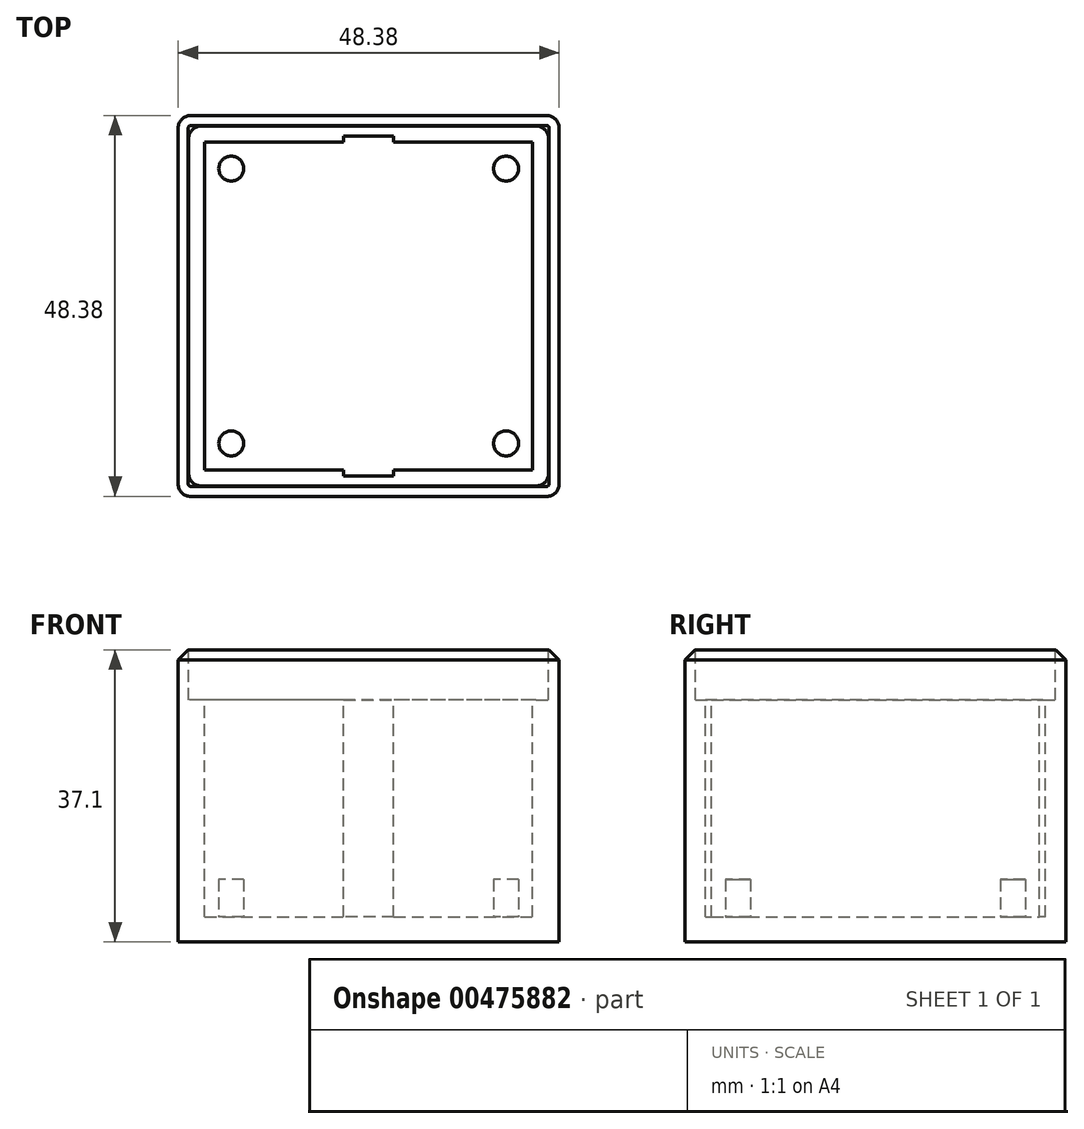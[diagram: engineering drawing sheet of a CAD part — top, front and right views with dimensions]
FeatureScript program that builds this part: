
annotation { "Feature Type Name" : "Feature", "Feature Type Description" : "" }
export const myFeature = defineFeature(function(context is Context, id is Id, definition is map)
    precondition{}
    {
        {
            var Q0;
            Q0=qCreatedBy(makeId("Top.planeOp"),FACE);
            var sketch = newSketch(context, id + "F0", { "sketchPlane" : qUnion([Q0])});
            skLineSegment(sketch, "E0.bottom", {"start": v(22.6, 24.2) * mm, "end": v(-22.6, 24.2) * mm});
            skLineSegment(sketch, "E0.top", {"start": v(22.6, -24.2) * mm, "end": v(-22.6, -24.2) * mm});
            skLineSegment(sketch, "E0.left", {"start": v(24.2, 22.6) * mm, "end": v(24.2, -22.6) * mm});
            skLineSegment(sketch, "E0.right", {"start": v(-24.2, 22.6) * mm, "end": v(-24.2, -22.6) * mm});
            skPoint(sketch, "E0.middle", {"position": v(0, 0) * mm});
            skPoint(sketch, "E1.visualSharp", {"position": v(-24.2, 24.2) * mm});
            skArc(sketch, "E1.filletArc", {"start": v(-22.6, 24.2) * mm, "mid": v(-23.73, 23.73) * mm, "end": v(-24.2, 22.6) * mm});
            skPoint(sketch, "E2.visualSharp", {"position": v(24.2, 24.2) * mm});
            skArc(sketch, "E2.filletArc", {"start": v(24.2, 22.6) * mm, "mid": v(23.73, 23.73) * mm, "end": v(22.6, 24.2) * mm});
            skPoint(sketch, "E3.visualSharp", {"position": v(24.2, -24.2) * mm});
            skArc(sketch, "E3.filletArc", {"start": v(22.6, -24.2) * mm, "mid": v(23.73, -23.73) * mm, "end": v(24.2, -22.6) * mm});
            skPoint(sketch, "E4.visualSharp", {"position": v(-24.2, -24.2) * mm});
            skArc(sketch, "E4.filletArc", {"start": v(-24.2, -22.6) * mm, "mid": v(-23.73, -23.73) * mm, "end": v(-22.6, -24.2) * mm});
            skSolve(sketch);
        }
        {
            var Q0;
            Q0 = qSketchRegion(id + "F0", true);
            extrude(context, id + "F1", {"entities" : qUnion([Q0]), "endBound" : BoundingType.SYMMETRIC, "depth" : 37.1 * mm});
        }
        {
            var Q0;
            Q0=makeQuery(id+"F1.opExtrude","CAP_FACE",FACE,{"disambiguationData":[OSD([sQuery(id+"F0.wireOp",EDGE,"E0.bottom"),sQuery(id+"F0.wireOp",EDGE,"E0.top"),sQuery(id+"F0.wireOp",EDGE,"E0.left"),sQuery(id+"F0.wireOp",EDGE,"E0.right"),sQuery(id+"F0.wireOp",EDGE,"E1.filletArc"),sQuery(id+"F0.wireOp",EDGE,"E2.filletArc"),sQuery(id+"F0.wireOp",EDGE,"E3.filletArc"),sQuery(id+"F0.wireOp",EDGE,"E4.filletArc")])],"isStart":false});
            var sketch = newSketch(context, id + "F2", { "sketchPlane" : qUnion([Q0])});
            skLineSegment(sketch, "E5.1", {"start": v(20.83, 20.38) * mm, "end": v(20.83, -20.38) * mm});
            skLineSegment(sketch, "E5.2", {"start": v(20.38, 20.83) * mm, "end": v(-20.38, 20.83) * mm});
            skLineSegment(sketch, "E5.5", {"start": v(-20.83, 20.38) * mm, "end": v(-20.83, -20.38) * mm});
            skLineSegment(sketch, "E5.7", {"start": v(20.38, -20.83) * mm, "end": v(-20.38, -20.83) * mm});
            skLineSegment(sketch, "E6", {"start": v(-20.83, 20.38) * mm, "end": v(-20.83, 20.83) * mm});
            skLineSegment(sketch, "E7", {"start": v(-20.83, 20.83) * mm, "end": v(-20.38, 20.83) * mm});
            skLineSegment(sketch, "E8", {"start": v(20.38, 20.83) * mm, "end": v(20.83, 20.83) * mm});
            skLineSegment(sketch, "E9", {"start": v(20.83, 20.83) * mm, "end": v(20.83, 20.38) * mm});
            skLineSegment(sketch, "E10", {"start": v(20.83, -20.38) * mm, "end": v(20.83, -20.83) * mm});
            skLineSegment(sketch, "E11", {"start": v(20.83, -20.83) * mm, "end": v(20.38, -20.83) * mm});
            skLineSegment(sketch, "E12", {"start": v(-20.83, -20.38) * mm, "end": v(-20.83, -20.83) * mm});
            skLineSegment(sketch, "E13", {"start": v(-20.83, -20.83) * mm, "end": v(-20.38, -20.83) * mm});
            skSolve(sketch);
        }
        {
            var Q0;
            Q0 = qSketchRegion(id + "F2", true);
            extrude(context, id + "F3", {"entities" : qUnion([Q0]), "operationType" : NewBodyOperationType.REMOVE, "oppositeDirection" : true, "depth" : 33.93 * mm});
        }
        {
            var Q0;
            Q0=makeQuery(id+"F1.opExtrude","CAP_FACE",FACE,{"disambiguationData":[OSD([sQuery(id+"F0.wireOp",EDGE,"E0.bottom"),sQuery(id+"F0.wireOp",EDGE,"E0.top"),sQuery(id+"F0.wireOp",EDGE,"E0.left"),sQuery(id+"F0.wireOp",EDGE,"E0.right"),sQuery(id+"F0.wireOp",EDGE,"E1.filletArc"),sQuery(id+"F0.wireOp",EDGE,"E2.filletArc"),sQuery(id+"F0.wireOp",EDGE,"E3.filletArc"),sQuery(id+"F0.wireOp",EDGE,"E4.filletArc")])],"isStart":false});
            var sketch = newSketch(context, id + "F4", { "sketchPlane" : qUnion([Q0])});
            skLineSegment(sketch, "E14.bottom", {"start": v(22.86, 22.86) * mm, "end": v(-22.86, 22.86) * mm});
            skLineSegment(sketch, "E14.top", {"start": v(22.86, -22.86) * mm, "end": v(-22.86, -22.86) * mm});
            skLineSegment(sketch, "E14.left", {"start": v(22.86, 22.86) * mm, "end": v(22.86, -22.86) * mm});
            skLineSegment(sketch, "E14.right", {"start": v(-22.86, 22.86) * mm, "end": v(-22.86, -22.86) * mm});
            skPoint(sketch, "E14.middle", {"position": v(0, 0) * mm});
            skSolve(sketch);
        }
        {
            var Q0;
            Q0 = qSketchRegion(id + "F4", true);
            extrude(context, id + "F5", {"entities" : qUnion([Q0]), "operationType" : NewBodyOperationType.REMOVE, "oppositeDirection" : true, "depth" : 6.35 * mm});
        }
        {
            var Q0;
            {var subQ0=sQuery(id+"F2.wireOp",EDGE,"E5.7");var subQ1=sQuery(id+"F2.wireOp",EDGE,"E5.6");var subQ2=sQuery(id+"F2.wireOp",EDGE,"E5.5");var subQ3=sQuery(id+"F2.wireOp",EDGE,"E5.4");var subQ4=sQuery(id+"F2.wireOp",EDGE,"E5.3");var subQ5=sQuery(id+"F2.wireOp",EDGE,"E5.2");var subQ6=sQuery(id+"F2.wireOp",EDGE,"E5.1");var subQ7=sQuery(id+"F2.wireOp",EDGE,"E5.0");Q0=makeQuery(id+"F6M7IgCAsm79SRp_1.boolean.opBoolean","MERGE",FACE,{"derivedFrom":[makeQuery(id+"F3.boolean.opBoolean","COPY",FACE,{"derivedFrom":makeQuery(id+"F3.opExtrude","CAP_FACE",FACE,{"disambiguationData":[OSD([subQ7,subQ6,subQ5,subQ4,subQ3,subQ2,subQ1,subQ0])],"isStart":false})}),makeQuery(id+"F6M7IgCAsm79SRp_1.opExtrude","CAP_FACE",FACE,{"disambiguationData":[OSD([subQ7,subQ6,subQ5,subQ4,subQ3,subQ2,subQ1,subQ0]),ownerDisambiguation([makeQuery(id+"FmsYwUqMiXvRgAx_1.imprint","IMPRINT",EDGE,{"derivedFrom":sQuery(id+"FmsYwUqMiXvRgAx_1.wireOp",EDGE,"RRrNXNMf-GQmn-cS1J-N3Tq-7I37AppBpzz9.bottom")})])],"isStart":false}),makeQuery(id+"F6M7IgCAsm79SRp_1.opExtrude","CAP_FACE",FACE,{"disambiguationData":[OSD([subQ7,subQ6,subQ5,subQ4,subQ3,subQ2,subQ1,subQ0]),ownerDisambiguation([makeQuery(id+"FmsYwUqMiXvRgAx_1.imprint","IMPRINT",EDGE,{"derivedFrom":sQuery(id+"FmsYwUqMiXvRgAx_1.wireOp",EDGE,"797062fd-0b08-47d3-9a36-d671014024f00.MirrorCS")})])],"isStart":false})]});}
            var sketch = newSketch(context, id + "F6", { "sketchPlane" : qUnion([Q0])});
            skCircle(sketch, "E15", {"center": v(17.45, -17.45) * mm, "radius": 1.59 * mm});
            skCircle(sketch, "E16.MirrorC", {"center": v(-17.45, -17.45) * mm, "radius": 1.59 * mm});
            skCircle(sketch, "E17.MirrorC", {"center": v(-17.45, 17.45) * mm, "radius": 1.59 * mm});
            skCircle(sketch, "E18.MirrorC", {"center": v(17.45, 17.45) * mm, "radius": 1.59 * mm});
            skLineSegment(sketch, "E19", {"start": v(20.83, -20.83) * mm, "end": v(17.45, -17.45) * mm, "construction": true});
            skSolve(sketch);
        }
        {
            var Q0;
            Q0 = qSketchRegion(id + "F6", true);
            extrude(context, id + "F7", {"entities" : qUnion([Q0]), "operationType" : NewBodyOperationType.ADD, "depth" : 4.78 * mm});
        }
        {
            var Q0;
            Q0=makeQuery(id+"F5.boolean.opBoolean","COPY",EDGE,{"derivedFrom":makeQuery(id+"F5.opExtrude","SWEPT_EDGE",EDGE,{"disambiguationData":[OSD([sQuery(id+"F4.wireOp",EDGE,"E14.bottom"),sQuery(id+"F4.wireOp",EDGE,"E14.left")])]})});
            var Q1;
            Q1=makeQuery(id+"F5.boolean.opBoolean","COPY",EDGE,{"derivedFrom":makeQuery(id+"F5.opExtrude","SWEPT_EDGE",EDGE,{"disambiguationData":[OSD([sQuery(id+"F4.wireOp",EDGE,"E14.bottom"),sQuery(id+"F4.wireOp",EDGE,"E14.right")])]})});
            var Q2;
            Q2=makeQuery(id+"F5.boolean.opBoolean","COPY",EDGE,{"derivedFrom":makeQuery(id+"F5.opExtrude","SWEPT_EDGE",EDGE,{"disambiguationData":[OSD([sQuery(id+"F4.wireOp",EDGE,"E14.top"),sQuery(id+"F4.wireOp",EDGE,"E14.right")])]})});
            var Q3;
            Q3=makeQuery(id+"F5.boolean.opBoolean","COPY",EDGE,{"derivedFrom":makeQuery(id+"F5.opExtrude","SWEPT_EDGE",EDGE,{"disambiguationData":[OSD([sQuery(id+"F4.wireOp",EDGE,"E14.top"),sQuery(id+"F4.wireOp",EDGE,"E14.left")])]})});
            fillet(context, id + "F8", {"entities" : qUnion([Q0, Q1, Q2, Q3]), "radius" : 1.59 * mm, "tangentPropagation" : true, "allowEdgeOverflow" : false});
        }
        {
            var Q0;
            Q0=makeQuery(id+"F5.boolean.opBoolean","COPY",FACE,{"derivedFrom":makeQuery(id+"F5.opExtrude","CAP_FACE",FACE,{"disambiguationData":[OSD([sQuery(id+"F4.wireOp",EDGE,"E14.bottom"),sQuery(id+"F4.wireOp",EDGE,"E14.top"),sQuery(id+"F4.wireOp",EDGE,"E14.left"),sQuery(id+"F4.wireOp",EDGE,"E14.right")])],"isStart":false})});
            var sketch = newSketch(context, id + "F9", { "sketchPlane" : qUnion([Q0])});
            skLineSegment(sketch, "E20.bottom", {"start": v(-3.17, 20.83) * mm, "end": v(3.18, 20.83) * mm});
            skLineSegment(sketch, "E20.top", {"start": v(-3.17, 21.59) * mm, "end": v(3.17, 21.59) * mm});
            skLineSegment(sketch, "E20.left", {"start": v(-3.18, 20.83) * mm, "end": v(-3.18, 21.59) * mm});
            skLineSegment(sketch, "E20.right", {"start": v(3.18, 20.83) * mm, "end": v(3.18, 21.59) * mm});
            skLineSegment(sketch, "E21.MirrorCS", {"start": v(3.18, -20.83) * mm, "end": v(3.18, -21.59) * mm});
            skLineSegment(sketch, "E22.MirrorCS", {"start": v(-3.18, -20.83) * mm, "end": v(-3.18, -21.59) * mm});
            skLineSegment(sketch, "E23.MirrorCS", {"start": v(-3.17, -20.83) * mm, "end": v(3.18, -20.83) * mm});
            skLineSegment(sketch, "E24.MirrorCS", {"start": v(-3.17, -21.59) * mm, "end": v(3.17, -21.59) * mm});
            skSolve(sketch);
        }
        {
            var Q0;
            Q0 = qSketchRegion(id + "F9", true);
            var Q1;
            Q1=makeQuery(id+"F3.boolean.opBoolean","COPY",FACE,{"derivedFrom":makeQuery(id+"F3.opExtrude","CAP_FACE",FACE,{"disambiguationData":[OSD([sQuery(id+"F2.wireOp",EDGE,"E5.1"),sQuery(id+"F2.wireOp",EDGE,"E5.2"),sQuery(id+"F2.wireOp",EDGE,"E5.5"),sQuery(id+"F2.wireOp",EDGE,"E5.7"),sQuery(id+"F2.wireOp",EDGE,"E6"),sQuery(id+"F2.wireOp",EDGE,"E7"),sQuery(id+"F2.wireOp",EDGE,"E8"),sQuery(id+"F2.wireOp",EDGE,"E9"),sQuery(id+"F2.wireOp",EDGE,"E10"),sQuery(id+"F2.wireOp",EDGE,"E11"),sQuery(id+"F2.wireOp",EDGE,"E12"),sQuery(id+"F2.wireOp",EDGE,"E13")])],"isStart":false})});
            extrude(context, id + "F10", {"entities" : qUnion([Q0]), "operationType" : NewBodyOperationType.REMOVE, "endBound" : BoundingType.UP_TO_SURFACE, "oppositeDirection" : true, "endBoundEntityFace" : qUnion([Q1]), "depth" : 25.4 * mm});
        }
        {
            var Q0;
            Q0=makeQuery(id+"F1.opExtrude","CAP_EDGE",EDGE,{"disambiguationData":[OSD([sQuery(id+"F0.wireOp",EDGE,"E1.filletArc")])],"isStart":false});
            var Q1;
            Q1=makeQuery(id+"F1.opExtrude","CAP_EDGE",EDGE,{"disambiguationData":[OSD([sQuery(id+"F0.wireOp",EDGE,"E0.right")])],"isStart":false});
            var Q2;
            Q2=makeQuery(id+"F1.opExtrude","CAP_EDGE",EDGE,{"disambiguationData":[OSD([sQuery(id+"F0.wireOp",EDGE,"E4.filletArc")])],"isStart":false});
            var Q3;
            Q3=makeQuery(id+"F1.opExtrude","CAP_EDGE",EDGE,{"disambiguationData":[OSD([sQuery(id+"F0.wireOp",EDGE,"E0.top")])],"isStart":false});
            var Q4;
            Q4=makeQuery(id+"F1.opExtrude","CAP_EDGE",EDGE,{"disambiguationData":[OSD([sQuery(id+"F0.wireOp",EDGE,"E3.filletArc")])],"isStart":false});
            var Q5;
            Q5=makeQuery(id+"F1.opExtrude","CAP_EDGE",EDGE,{"disambiguationData":[OSD([sQuery(id+"F0.wireOp",EDGE,"E0.left")])],"isStart":false});
            var Q6;
            Q6=makeQuery(id+"F1.opExtrude","CAP_EDGE",EDGE,{"disambiguationData":[OSD([sQuery(id+"F0.wireOp",EDGE,"E0.bottom")])],"isStart":false});
            chamfer(context, id + "F11", {"entities" : qUnion([Q0, Q1, Q2, Q3, Q4, Q5, Q6]), "width" : 1.27 * mm, "tangentPropagation" : true});
        }
    });
